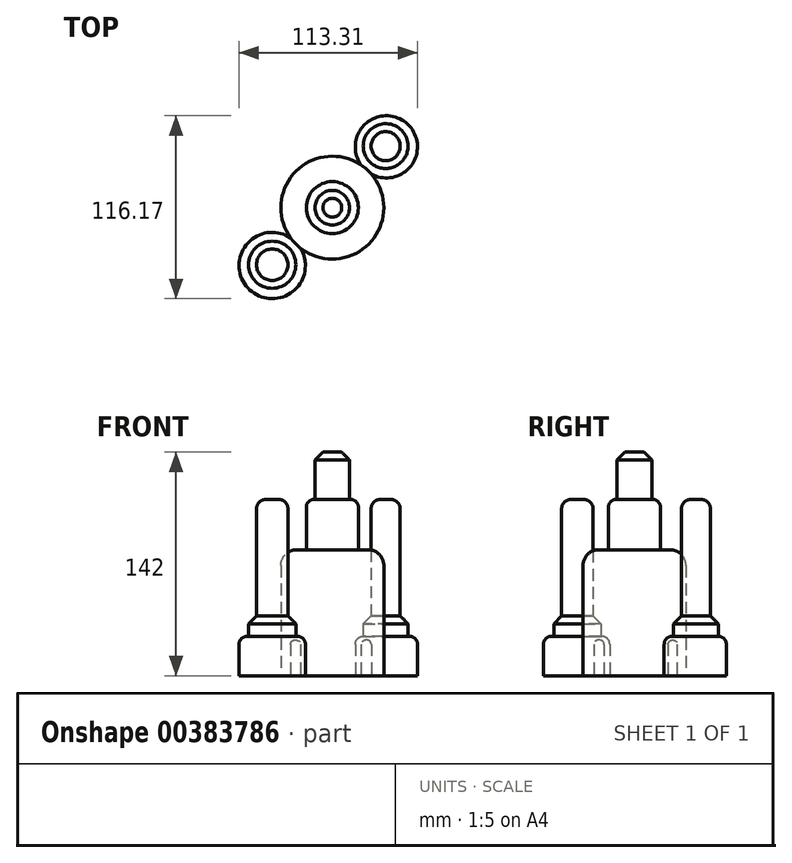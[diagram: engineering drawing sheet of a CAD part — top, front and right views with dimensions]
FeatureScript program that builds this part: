
annotation { "Feature Type Name" : "Feature", "Feature Type Description" : "" }
export const myFeature = defineFeature(function(context is Context, id is Id, definition is map)
    precondition{}
    {
        {
            var Q0;
            Q0=qCreatedBy(makeId("Top.planeOp"),FACE);
            var sketch = newSketch(context, id + "F0", { "sketchPlane" : qUnion([Q0])});
            skCircle(sketch, "E0", {"center": v(0, 0) * mm, "radius": 32.7 * mm});
            skSolve(sketch);
        }
        {
            var Q0;
            Q0=makeQuery(id+"F0.imprint","IMPRINT",FACE,{"disambiguationData":[TD([[makeQuery(id+"F0.imprint","IMPRINT",EDGE,{"derivedFrom":sQuery(id+"F0.wireOp",EDGE,"E0")}),1.0]])]});
            extrude(context, id + "F1", {"entities" : qUnion([Q0]), "depth" : 80 * mm});
        }
        {
            var Q0;
            Q0=makeQuery(id+"F1.opExtrude","CAP_FACE",FACE,{"disambiguationData":[OSD([sQuery(id+"F0.wireOp",EDGE,"E0")])],"isStart":false});
            fillet(context, id + "F2", {"entities" : qUnion([Q0]), "radius" : 10 * mm, "tangentPropagation" : true, "allowEdgeOverflow" : false});
        }
        {
            var Q0;
            Q0=makeQuery(id+"F1.opExtrude","CAP_FACE",FACE,{"disambiguationData":[OSD([sQuery(id+"F0.wireOp",EDGE,"E0")])],"isStart":false});
            var sketch = newSketch(context, id + "F3", { "sketchPlane" : qUnion([Q0])});
            skCircle(sketch, "E1", {"center": v(0, 0) * mm, "radius": 16.52 * mm});
            skSolve(sketch);
        }
        {
            var Q0;
            Q0 = qSketchRegion(id + "F3", true);
            extrude(context, id + "F4", {"entities" : qUnion([Q0]), "operationType" : NewBodyOperationType.ADD, "depth" : 32 * mm});
        }
        {
            var Q0;
            Q0=makeQuery(id+"F4.opExtrude","CAP_FACE",FACE,{"disambiguationData":[OSD([sQuery(id+"F3.wireOp",EDGE,"E1")])],"isStart":false});
            fillet(context, id + "F5", {"entities" : qUnion([Q0]), "radius" : 5 * mm, "tangentPropagation" : true, "allowEdgeOverflow" : false});
        }
        {
            var Q0;
            Q0=makeQuery(id+"F4.opExtrude","CAP_FACE",FACE,{"disambiguationData":[OSD([sQuery(id+"F3.wireOp",EDGE,"E1")])],"isStart":false});
            var sketch = newSketch(context, id + "F6", { "sketchPlane" : qUnion([Q0])});
            skCircle(sketch, "E2", {"center": v(0, 0) * mm, "radius": 10.98 * mm});
            skSolve(sketch);
        }
        {
            var Q0;
            Q0 = qSketchRegion(id + "F6", true);
            extrude(context, id + "F7", {"entities" : qUnion([Q0]), "operationType" : NewBodyOperationType.ADD, "depth" : 30 * mm});
        }
        {
            var Q0;
            Q0=makeQuery(id+"F7.opExtrude","CAP_EDGE",EDGE,{"disambiguationData":[OSD([sQuery(id+"F6.wireOp",EDGE,"E2")])],"isStart":false});
            chamfer(context, id + "F8", {"entities" : qUnion([Q0]), "width" : 5 * mm, "tangentPropagation" : true});
        }
        {
            var Q0;
            Q0=qCreatedBy(makeId("Top.planeOp"),FACE);
            var sketch = newSketch(context, id + "F9", { "sketchPlane" : qUnion([Q0])});
            skCircle(sketch, "E3", {"center": v(34.34, 38.64) * mm, "radius": 19.75 * mm});
            skSolve(sketch);
        }
        {
            var Q0;
            Q0=makeQuery(id+"F9.imprint","IMPRINT",FACE,{"disambiguationData":[TD([[makeQuery(id+"F9.imprint","IMPRINT",EDGE,{"derivedFrom":sQuery(id+"F9.wireOp",EDGE,"E3")}),1.0]])]});
            extrude(context, id + "F10", {"entities" : qUnion([Q0]), "operationType" : NewBodyOperationType.ADD, "depth" : 25 * mm});
        }
        {
            var Q0;
            Q0=qCreatedBy(makeId("Top.planeOp"),FACE);
            var sketch = newSketch(context, id + "F11", { "sketchPlane" : qUnion([Q0])});
            skCircle(sketch, "E4", {"center": v(-38.16, -36.73) * mm, "radius": 21.06 * mm});
            skSolve(sketch);
        }
        {
            var Q0;
            Q0=makeQuery(id+"F11.imprint","IMPRINT",FACE,{"disambiguationData":[TD([[makeQuery(id+"F11.imprint","IMPRINT",EDGE,{"derivedFrom":sQuery(id+"F11.wireOp",EDGE,"E4")}),1.0]])]});
            extrude(context, id + "F12", {"entities" : qUnion([Q0]), "operationType" : NewBodyOperationType.ADD, "depth" : 25 * mm});
        }
        {
            var Q0;
            Q0=qCreatedBy(makeId("Top.planeOp"),FACE);
            var sketch = newSketch(context, id + "F13", { "sketchPlane" : qUnion([Q0])});
            skCircle(sketch, "E5", {"center": v(-38.16, -36.25) * mm, "radius": 14.98 * mm});
            skCircle(sketch, "E6", {"center": v(33.87, 39.11) * mm, "radius": 14.23 * mm});
            skSolve(sketch);
        }
        {
            var Q0;
            Q0 = qSketchRegion(id + "F13", true);
            extrude(context, id + "F14", {"entities" : qUnion([Q0]), "operationType" : NewBodyOperationType.ADD, "depth" : 38 * mm});
        }
        {
            var Q0;
            Q0=makeQuery(id+"F12.opExtrude","CAP_EDGE",EDGE,{"disambiguationData":[OSD([sQuery(id+"F11.wireOp",EDGE,"E4")])],"isStart":false});
            var Q1;
            Q1=makeQuery(id+"F10.opExtrude","CAP_EDGE",EDGE,{"disambiguationData":[OSD([sQuery(id+"F9.wireOp",EDGE,"E3")])],"isStart":false});
            fillet(context, id + "F15", {"entities" : qUnion([Q0, Q1]), "radius" : 5 * mm, "tangentPropagation" : true, "allowEdgeOverflow" : false});
        }
        {
            var Q0;
            Q0=makeQuery(id+"F14.opExtrude","CAP_EDGE",EDGE,{"disambiguationData":[OSD([sQuery(id+"F13.wireOp",EDGE,"E6")])],"isStart":false});
            var Q1;
            Q1=makeQuery(id+"F14.opExtrude","CAP_EDGE",EDGE,{"disambiguationData":[OSD([sQuery(id+"F13.wireOp",EDGE,"E5")])],"isStart":false});
            chamfer(context, id + "F16", {"entities" : qUnion([Q0, Q1]), "width" : 5 * mm, "tangentPropagation" : true});
        }
        {
            var Q0;
            Q0=makeQuery(id+"F14.opExtrude","CAP_FACE",FACE,{"disambiguationData":[OSD([sQuery(id+"F13.wireOp",EDGE,"E5")])],"isStart":false});
            var Q1;
            Q1=makeQuery(id+"F14.opExtrude","CAP_FACE",FACE,{"disambiguationData":[OSD([sQuery(id+"F13.wireOp",EDGE,"E6")])],"isStart":false});
            extrude(context, id + "F17", {"entities" : qUnion([Q0, Q1]), "operationType" : NewBodyOperationType.ADD, "depth" : 74 * mm});
        }
        {
            var Q0;
            Q0=makeQuery(id+"F17.opExtrude","CAP_EDGE",EDGE,{"disambiguationData":[OSD([sQuery(id+"F13.wireOp",EDGE,"E6")])],"isStart":false});
            var Q1;
            Q1=makeQuery(id+"F17.opExtrude","CAP_FACE",FACE,{"disambiguationData":[OSD([sQuery(id+"F13.wireOp",EDGE,"E5")])],"isStart":false});
            fillet(context, id + "F18", {"entities" : qUnion([Q0, Q1]), "radius" : 6 * mm, "tangentPropagation" : true, "allowEdgeOverflow" : false});
        }
    });
